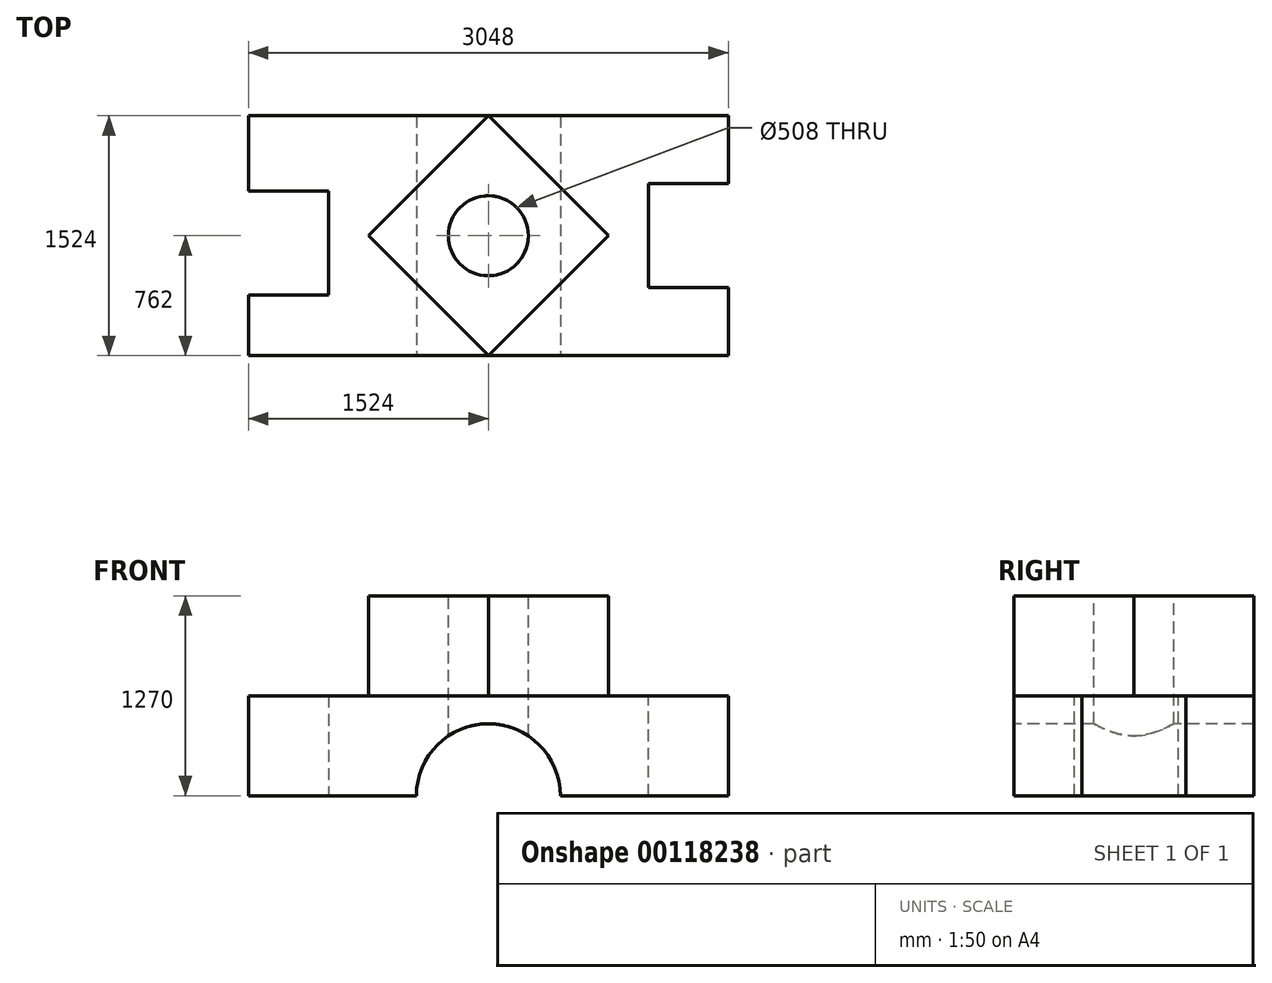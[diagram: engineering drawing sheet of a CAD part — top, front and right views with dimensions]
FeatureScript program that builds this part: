
annotation { "Feature Type Name" : "Feature", "Feature Type Description" : "" }
export const myFeature = defineFeature(function(context is Context, id is Id, definition is map)
    precondition{}
    {
        {
            var Q0;
            Q0=qCreatedBy(makeId("Top.planeOp"),FACE);
            var sketch = newSketch(context, id + "F0", { "sketchPlane" : qUnion([Q0])});
            skLineSegment(sketch, "E0.bottom", {"start": v(1524, -762) * mm, "end": v(-1524, -762) * mm});
            skLineSegment(sketch, "E0.top", {"start": v(1524, 762) * mm, "end": v(-1524, 762) * mm});
            skLineSegment(sketch, "E0.left", {"start": v(1524, -762) * mm, "end": v(1524, 762) * mm});
            skLineSegment(sketch, "E0.right", {"start": v(-1524, -762) * mm, "end": v(-1524, 762) * mm});
            skPoint(sketch, "E0.middle", {"position": v(0, 0) * mm});
            skSolve(sketch);
        }
        {
            var Q0;
            Q0 = qSketchRegion(id + "F0", true);
            extrude(context, id + "F1", {"entities" : qUnion([Q0]), "depth" : 635 * mm});
        }
        {
            var Q0;
            Q0=makeQuery(id+"F1.opExtrude","CAP_FACE",FACE,{"disambiguationData":[OSD([sQuery(id+"F0.wireOp",EDGE,"E0.bottom"),sQuery(id+"F0.wireOp",EDGE,"E0.top"),sQuery(id+"F0.wireOp",EDGE,"E0.left"),sQuery(id+"F0.wireOp",EDGE,"E0.right")])],"isStart":false});
            var sketch = newSketch(context, id + "F2", { "sketchPlane" : qUnion([Q0])});
            skLineSegment(sketch, "E1", {"start": v(0, 762) * mm, "end": v(-762, 0) * mm});
            skLineSegment(sketch, "E2", {"start": v(-762, 0) * mm, "end": v(0, -762) * mm});
            skLineSegment(sketch, "E3", {"start": v(0, -762) * mm, "end": v(762, 0) * mm});
            skLineSegment(sketch, "E4", {"start": v(762, 0) * mm, "end": v(0, 762) * mm});
            skSolve(sketch);
        }
        {
            var Q0;
            Q0 = qSketchRegion(id + "F2", true);
            extrude(context, id + "F3", {"entities" : qUnion([Q0]), "operationType" : NewBodyOperationType.ADD, "depth" : 635 * mm});
        }
        {
            var Q0;
            Q0=makeQuery(id+"F1.opExtrude","CAP_FACE",FACE,{"disambiguationData":[OSD([sQuery(id+"F0.wireOp",EDGE,"E0.bottom"),sQuery(id+"F0.wireOp",EDGE,"E0.top"),sQuery(id+"F0.wireOp",EDGE,"E0.left"),sQuery(id+"F0.wireOp",EDGE,"E0.right")])],"isStart":true});
            var sketch = newSketch(context, id + "F4", { "sketchPlane" : qUnion([Q0])});
            skLineSegment(sketch, "E5.bottom", {"start": v(-1016, -282.5) * mm, "end": v(-2032, -282.5) * mm});
            skLineSegment(sketch, "E5.top", {"start": v(-1016, 377.9) * mm, "end": v(-2032, 377.9) * mm});
            skLineSegment(sketch, "E5.left", {"start": v(-1016, -282.5) * mm, "end": v(-1016, 377.9) * mm});
            skLineSegment(sketch, "E5.right", {"start": v(-2032, -282.5) * mm, "end": v(-2032, 377.9) * mm});
            skPoint(sketch, "E5.middle", {"position": v(-1524, 47.7) * mm});
            skSolve(sketch);
        }
        {
            var Q0;
            Q0 = qSketchRegion(id + "F4", true);
            extrude(context, id + "F5", {"entities" : qUnion([Q0]), "operationType" : NewBodyOperationType.REMOVE, "oppositeDirection" : true, "depth" : 986.63 * mm});
        }
        {
            var Q0;
            {var subQ0=sQuery(id+"F0.wireOp",EDGE,"E0.left");var subQ1=sQuery(id+"F0.wireOp",EDGE,"E0.top");var subQ2=sQuery(id+"F0.wireOp",EDGE,"E0.bottom");var subQ3=makeQuery(id+"F1.opExtrude","CAP_FACE",FACE,{"disambiguationData":[OSD([subQ2,subQ1,subQ0,sQuery(id+"F0.wireOp",EDGE,"E0.right")])],"isStart":false});Q0=makeQuery(id+"F3.boolean.opBoolean","SPLIT",FACE,{"disambiguationData":[TD([makeQuery(id+"F1.opExtrude","SWEPT_FACE",FACE,{"disambiguationData":[OSD([subQ0])]})])],"derivedFrom":subQ3});}
            var sketch = newSketch(context, id + "F6", { "sketchPlane" : qUnion([Q0])});
            skLineSegment(sketch, "E6.bottom", {"start": v(1016, -330.2) * mm, "end": v(2032, -330.2) * mm});
            skLineSegment(sketch, "E6.top", {"start": v(1016, 330.2) * mm, "end": v(2032, 330.2) * mm});
            skLineSegment(sketch, "E6.left", {"start": v(1016, -330.2) * mm, "end": v(1016, 330.2) * mm});
            skLineSegment(sketch, "E6.right", {"start": v(2032, -330.2) * mm, "end": v(2032, 330.2) * mm});
            skPoint(sketch, "E6.middle", {"position": v(1524, 0) * mm});
            skSolve(sketch);
        }
        {
            var Q0;
            Q0 = qSketchRegion(id + "F6", true);
            extrude(context, id + "F7", {"entities" : qUnion([Q0]), "operationType" : NewBodyOperationType.REMOVE, "endBound" : BoundingType.THROUGH_ALL, "oppositeDirection" : true, "depth" : 25.4 * mm});
        }
        {
            var Q0;
            Q0=makeQuery(id+"F1.opExtrude","SWEPT_FACE",FACE,{"disambiguationData":[OSD([sQuery(id+"F0.wireOp",EDGE,"E0.bottom")])]});
            var sketch = newSketch(context, id + "F8", { "sketchPlane" : qUnion([Q0])});
            skCircle(sketch, "E7", {"center": v(0, 0) * mm, "radius": 457.2 * mm});
            skSolve(sketch);
        }
        {
            var Q0;
            Q0 = qSketchRegion(id + "F8", true);
            extrude(context, id + "F9", {"entities" : qUnion([Q0]), "operationType" : NewBodyOperationType.REMOVE, "endBound" : BoundingType.THROUGH_ALL, "oppositeDirection" : true, "depth" : 25.4 * mm});
        }
        {
            var Q0;
            Q0=makeQuery(id+"F3.opExtrude","CAP_FACE",FACE,{"disambiguationData":[OSD([sQuery(id+"F2.wireOp",EDGE,"E1"),sQuery(id+"F2.wireOp",EDGE,"E2"),sQuery(id+"F2.wireOp",EDGE,"E3"),sQuery(id+"F2.wireOp",EDGE,"E4")])],"isStart":false});
            var sketch = newSketch(context, id + "F10", { "sketchPlane" : qUnion([Q0])});
            skCircle(sketch, "E8", {"center": v(0, 0) * mm, "radius": 254 * mm});
            skSolve(sketch);
        }
        {
            var Q0;
            Q0 = qSketchRegion(id + "F10", true);
            extrude(context, id + "F11", {"entities" : qUnion([Q0]), "operationType" : NewBodyOperationType.REMOVE, "endBound" : BoundingType.THROUGH_ALL, "oppositeDirection" : true, "depth" : 25.4 * mm});
        }
    });
